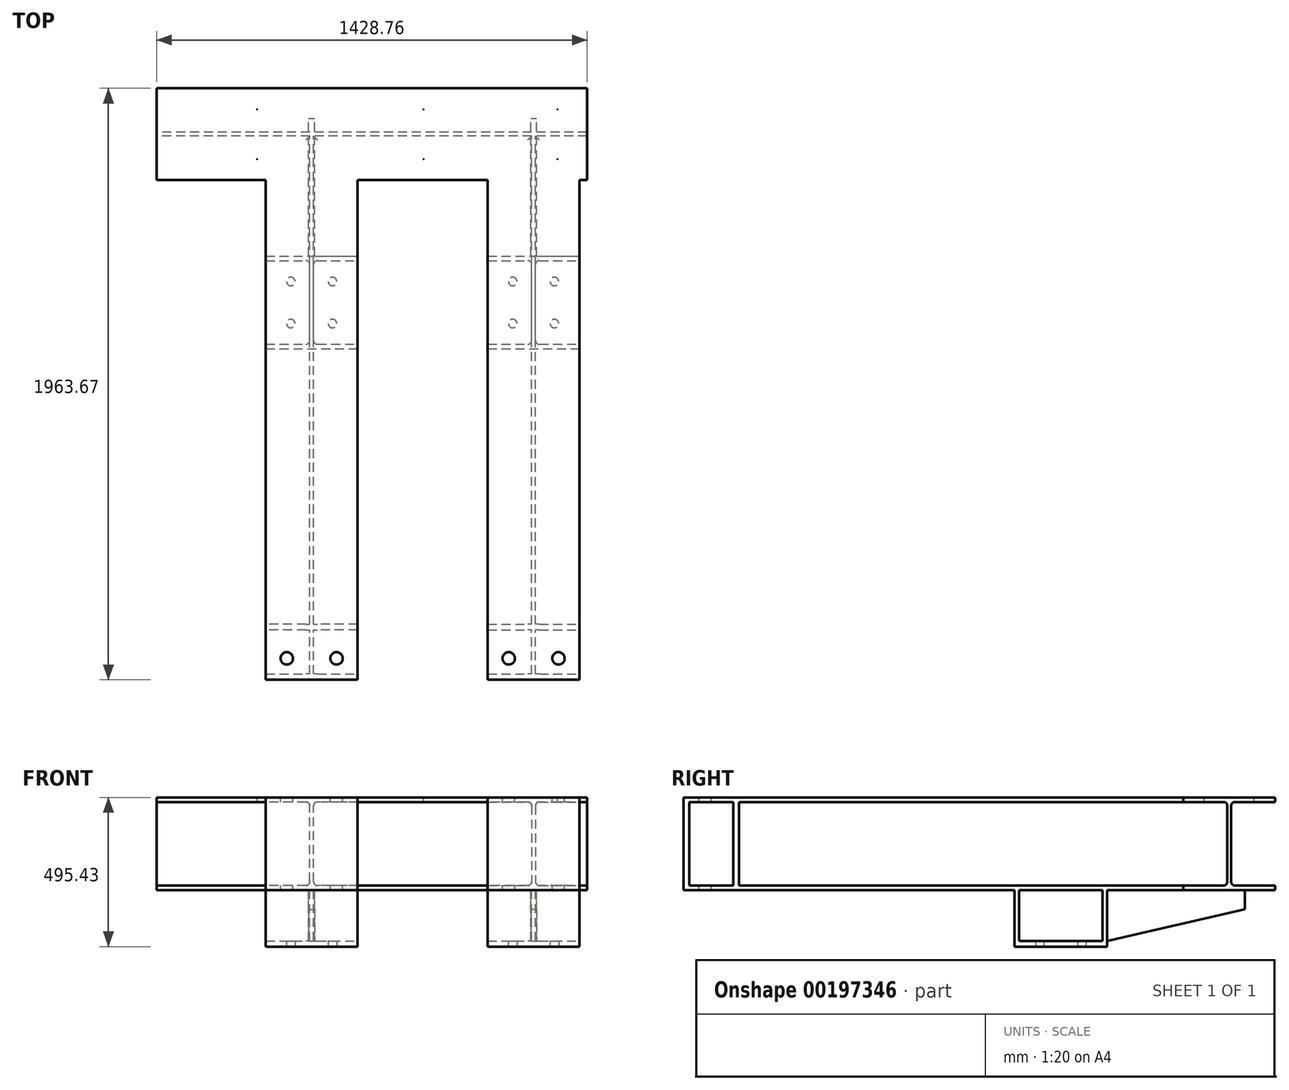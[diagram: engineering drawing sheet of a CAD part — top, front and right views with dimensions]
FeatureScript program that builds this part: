
annotation { "Feature Type Name" : "Feature", "Feature Type Description" : "" }
export const myFeature = defineFeature(function(context is Context, id is Id, definition is map)
    precondition{}
    {
        {
            var Q0;
            Q0=qCreatedBy(makeId("Right.planeOp"),FACE);
            var sketch = newSketch(context, id + "F0", { "sketchPlane" : qUnion([Q0])});
            skLineSegment(sketch, "E0.bottom", {"start": v(-152.4, 153.99) * mm, "end": v(152.4, 153.99) * mm});
            skLineSegment(sketch, "E0.top", {"start": v(-152.4, -153.99) * mm, "end": v(152.4, -153.99) * mm});
            skLineSegment(sketch, "E0.left", {"start": v(-152.4, 153.99) * mm, "end": v(-152.4, 138.75) * mm});
            skLineSegment(sketch, "E0.right", {"start": v(152.4, 153.99) * mm, "end": v(152.4, 138.75) * mm});
            skPoint(sketch, "E0.middle", {"position": v(0, 0) * mm});
            skLineSegment(sketch, "E1.0", {"start": v(-152.4, 138.75) * mm, "end": v(-19.05, 138.75) * mm});
            skLineSegment(sketch, "E2", {"start": v(-217.51, 0) * mm, "end": v(206.8, 0) * mm, "construction": true});
            skPoint(sketch, "E2.startSnap0", {"position": v(-152.4, 0) * mm});
            skLineSegment(sketch, "E3.MirrorCS", {"start": v(-152.4, -138.75) * mm, "end": v(-19.05, -138.75) * mm});
            skLineSegment(sketch, "E4", {"start": v(0, 208.18) * mm, "end": v(0, -222.4) * mm, "construction": true});
            skLineSegment(sketch, "E5.0", {"start": v(-6.35, 126.05) * mm, "end": v(-6.35, -126.05) * mm});
            skLineSegment(sketch, "E6.MirrorCS", {"start": v(6.35, 126.05) * mm, "end": v(6.35, -126.05) * mm});
            skPoint(sketch, "E7.orphan", {"position": v(-6.35, 208.18) * mm});
            skPoint(sketch, "E8.orphan", {"position": v(6.35, 208.18) * mm});
            skLineSegment(sketch, "E9.trimOffspring", {"start": v(19.05, 138.75) * mm, "end": v(152.4, 138.75) * mm});
            skPoint(sketch, "E10.orphan", {"position": v(6.35, -222.4) * mm});
            skLineSegment(sketch, "E11.trimOffspring", {"start": v(19.05, -138.75) * mm, "end": v(152.4, -138.75) * mm});
            skPoint(sketch, "E12.trimOffspring.end.orphan", {"position": v(-6.35, -222.4) * mm});
            skLineSegment(sketch, "E13.trimOffspring", {"start": v(152.4, -138.75) * mm, "end": v(152.4, -153.99) * mm});
            skLineSegment(sketch, "E14.trimOffspring", {"start": v(-152.4, -138.75) * mm, "end": v(-152.4, -153.99) * mm});
            skArc(sketch, "E15.filletArc", {"start": v(-6.35, 126.05) * mm, "mid": v(-10.07, 135.03) * mm, "end": v(-19.05, 138.75) * mm});
            skPoint(sketch, "E16.visualSharp", {"position": v(6.35, 138.75) * mm});
            skArc(sketch, "E16.filletArc", {"start": v(19.05, 138.75) * mm, "mid": v(10.07, 135.03) * mm, "end": v(6.35, 126.05) * mm});
            skPoint(sketch, "E17.visualSharp", {"position": v(6.35, -138.75) * mm});
            skArc(sketch, "E17.filletArc", {"start": v(6.35, -126.05) * mm, "mid": v(10.07, -135.03) * mm, "end": v(19.05, -138.75) * mm});
            skArc(sketch, "E18.filletArc", {"start": v(-19.05, -138.75) * mm, "mid": v(-10.07, -135.03) * mm, "end": v(-6.35, -126.05) * mm});
            skSolve(sketch);
        }
        {
            var Q0;
            Q0 = qSketchRegion(id + "F0", true);
            extrude(context, id + "F1", {"entities" : qUnion([Q0]), "endBound" : BoundingType.SYMMETRIC, "depth" : 1428.75 * mm});
        }
        {
            var Q0;
            Q0=makeQuery(id+"F1.opExtrude","SWEPT_FACE",FACE,{"disambiguationData":[OSD([sQuery(id+"F0.wireOp",EDGE,"E0.bottom")])]});
            var sketch = newSketch(context, id + "F2", { "sketchPlane" : qUnion([Q0])});
            skLineSegment(sketch, "E19.0", {"start": v(-714.38, -152.4) * mm, "end": v(-714.38, 152.4) * mm, "construction": true});
            skLineSegment(sketch, "E20", {"start": v(-714.38, 0) * mm, "end": v(783.99, 0) * mm, "construction": true});
            skLineSegment(sketch, "E21.0", {"start": v(-381, -152.4) * mm, "end": v(-381, 152.4) * mm, "construction": true});
            skLineSegment(sketch, "E22.0", {"start": v(171.45, -152.4) * mm, "end": v(171.45, 152.4) * mm, "construction": true});
            skLineSegment(sketch, "E23.0", {"start": v(615.95, -152.4) * mm, "end": v(615.95, 152.4) * mm, "construction": true});
            skLineSegment(sketch, "E24.0", {"start": v(-714.38, -82.55) * mm, "end": v(783.99, -82.55) * mm, "construction": true});
            skPoint(sketch, "E25", {"position": v(-381, -82.55) * mm});
            skPoint(sketch, "E26", {"position": v(171.45, -82.55) * mm});
            skPoint(sketch, "E27", {"position": v(615.95, -82.55) * mm});
            skPoint(sketch, "E28.MirrorP", {"position": v(615.95, 82.55) * mm});
            skPoint(sketch, "E29.MirrorP", {"position": v(171.45, 82.55) * mm});
            skPoint(sketch, "E30.MirrorP", {"position": v(-381, 82.55) * mm});
            skSolve(sketch);
        }
        {
            var Q0;
            Q0=sQuery(id+"F2.wireOp",VERTEX,"E30.MirrorP");
            var Q1;
            Q1=sQuery(id+"F2.wireOp",VERTEX,"E25");
            var Q2;
            Q2=sQuery(id+"F2.wireOp",VERTEX,"E29.MirrorP");
            var Q3;
            Q3=sQuery(id+"F2.wireOp",VERTEX,"E26");
            var Q4;
            Q4=sQuery(id+"F2.wireOp",VERTEX,"E28.MirrorP");
            var Q5;
            Q5=sQuery(id+"F2.wireOp",VERTEX,"E27");
            var Q6;
            Q6=makeQuery(id+"F1.opExtrude","SWEPT_BODY",BODY,{"disambiguationData":[OSD([sQuery(id+"F0.wireOp",EDGE,"E0.bottom"),sQuery(id+"F0.wireOp",EDGE,"E0.top"),sQuery(id+"F0.wireOp",EDGE,"E0.left"),sQuery(id+"F0.wireOp",EDGE,"E0.right"),sQuery(id+"F0.wireOp",EDGE,"E1.0"),sQuery(id+"F0.wireOp",EDGE,"E3.MirrorCS"),sQuery(id+"F0.wireOp",EDGE,"E5.0"),sQuery(id+"F0.wireOp",EDGE,"E6.MirrorCS"),sQuery(id+"F0.wireOp",EDGE,"E9.trimOffspring"),sQuery(id+"F0.wireOp",EDGE,"E11.trimOffspring"),sQuery(id+"F0.wireOp",EDGE,"E13.trimOffspring"),sQuery(id+"F0.wireOp",EDGE,"E14.trimOffspring"),sQuery(id+"F0.wireOp",EDGE,"E15.filletArc"),sQuery(id+"F0.wireOp",EDGE,"E16.filletArc"),sQuery(id+"F0.wireOp",EDGE,"E17.filletArc"),sQuery(id+"F0.wireOp",EDGE,"E18.filletArc")])]});
            hole(context, id + "F3", {"style" : HoleStyle.SIMPLE, "endStyle" : HoleEndStyle.BLIND, "standardTappedOrClearance" : lookupTablePath({ "standard" : "ANSI", "size" : "7/8", "type" : "Drilled" }), "standardBlindInLast" : lookupTablePath({ "standard" : "ANSI", "size" : "7/8", "type" : "Drilled" }), "holeDiameter" : 7 / 203.2 * mm, "holeDepth" : 76.2 * mm, "locations" : qUnion([Q0, Q1, Q2, Q3, Q4, Q5]), "scope" : qUnion([Q6])});
        }
        {
            var Q0;
            Q0=qCreatedBy(makeId("Front.planeOp"),FACE);
            var sketch = newSketch(context, id + "F4", { "sketchPlane" : qUnion([Q0])});
            skLineSegment(sketch, "E31.0", {"start": v(-714.38, 126.05) * mm, "end": v(-714.38, -126.05) * mm, "construction": true});
            skLineSegment(sketch, "E32.0", {"start": v(714.38, 138.75) * mm, "end": v(-193.68, 138.75) * mm, "construction": true});
            skLineSegment(sketch, "E33.0", {"start": v(714.38, -138.75) * mm, "end": v(-193.68, -138.75) * mm, "construction": true});
            skLineSegment(sketch, "E34.0", {"start": v(714.38, -153.99) * mm, "end": v(-714.38, -153.99) * mm, "construction": true});
            skLineSegment(sketch, "E35.0", {"start": v(714.38, 153.99) * mm, "end": v(-714.38, 153.99) * mm, "construction": true});
            skLineSegment(sketch, "E36", {"start": v(-714.38, 0) * mm, "end": v(832.86, 0) * mm, "construction": true});
            skPoint(sketch, "E36.endSnap0", {"position": v(-714.38, 0) * mm});
            skLineSegment(sketch, "E37.0", {"start": v(-200.03, 126.05) * mm, "end": v(-200.03, -126.05) * mm, "construction": true});
            skLineSegment(sketch, "E38.0", {"start": v(536.58, 126.05) * mm, "end": v(536.58, -126.05) * mm, "construction": true});
            skLineSegment(sketch, "E39.bottom", {"start": v(-352.43, 153.99) * mm, "end": v(-47.62, 153.99) * mm});
            skLineSegment(sketch, "E39.top", {"start": v(-352.43, -153.99) * mm, "end": v(-47.62, -153.99) * mm});
            skLineSegment(sketch, "E39.left", {"start": v(-352.43, 153.99) * mm, "end": v(-352.43, 138.75) * mm});
            skLineSegment(sketch, "E39.right", {"start": v(-47.62, 153.99) * mm, "end": v(-47.62, 138.75) * mm});
            skPoint(sketch, "E39.middle", {"position": v(-200.03, 0) * mm});
            skLineSegment(sketch, "E40", {"start": v(-352.43, 138.75) * mm, "end": v(-219.07, 138.75) * mm});
            skLineSegment(sketch, "E41", {"start": v(-352.43, -138.75) * mm, "end": v(-219.07, -138.75) * mm});
            skLineSegment(sketch, "E42.0", {"start": v(-206.38, 126.05) * mm, "end": v(-206.38, -126.05) * mm});
            skLineSegment(sketch, "E43.MirrorCS", {"start": v(-193.68, 126.05) * mm, "end": v(-193.68, -126.05) * mm});
            skLineSegment(sketch, "E44.trimOffspring", {"start": v(-47.62, -138.75) * mm, "end": v(-180.98, -138.75) * mm, "construction": true});
            skPoint(sketch, "E45.visualSharp", {"position": v(-206.38, 138.75) * mm});
            skArc(sketch, "E45.filletArc", {"start": v(-206.38, 126.05) * mm, "mid": v(-210.1, 135.03) * mm, "end": v(-219.07, 138.75) * mm});
            skPoint(sketch, "E46.orphan", {"position": v(-714.38, 138.75) * mm});
            skPoint(sketch, "E47.orphan", {"position": v(-714.38, -138.75) * mm});
            skLineSegment(sketch, "E48.trimOffspring", {"start": v(-180.98, 138.75) * mm, "end": v(-47.62, 138.75) * mm, "construction": true});
            skLineSegment(sketch, "E49.trimOffspring", {"start": v(-193.68, 138.75) * mm, "end": v(-47.62, 138.75) * mm});
            skLineSegment(sketch, "E50.trimOffspring", {"start": v(-193.68, -138.75) * mm, "end": v(-47.62, -138.75) * mm});
            skPoint(sketch, "E51.visualSharp", {"position": v(-206.38, -138.75) * mm});
            skArc(sketch, "E51.filletArc", {"start": v(-219.07, -138.75) * mm, "mid": v(-210.1, -135.03) * mm, "end": v(-206.38, -126.05) * mm});
            skPoint(sketch, "E52.visualSharp", {"position": v(-193.68, -138.75) * mm});
            skArc(sketch, "E52.filletArc", {"start": v(-193.68, -126.05) * mm, "mid": v(-189.96, -135.03) * mm, "end": v(-180.98, -138.75) * mm});
            skPoint(sketch, "E53.visualSharp", {"position": v(-193.68, 138.75) * mm});
            skArc(sketch, "E53.filletArc", {"start": v(-180.98, 138.75) * mm, "mid": v(-189.96, 135.03) * mm, "end": v(-193.68, 126.05) * mm});
            skLineSegment(sketch, "E54.trimOffspring", {"start": v(-352.43, 0) * mm, "end": v(-352.43, -153.99) * mm});
            skLineSegment(sketch, "E55.trimOffspring", {"start": v(-47.62, 0) * mm, "end": v(-47.62, -153.99) * mm});
            skLineSegment(sketch, "E56.1.0.0", {"start": v(384.17, 153.99) * mm, "end": v(688.97, 153.99) * mm});
            skLineSegment(sketch, "E56.1.0.1", {"start": v(384.17, 0) * mm, "end": v(384.17, -153.99) * mm});
            skLineSegment(sketch, "E56.1.0.2", {"start": v(542.92, 126.05) * mm, "end": v(542.92, -126.05) * mm});
            skLineSegment(sketch, "E56.1.0.3", {"start": v(384.17, -138.75) * mm, "end": v(517.52, -138.75) * mm});
            skLineSegment(sketch, "E56.1.0.4", {"start": v(530.22, 126.05) * mm, "end": v(530.22, -126.05) * mm});
            skLineSegment(sketch, "E56.1.0.5", {"start": v(555.62, 138.75) * mm, "end": v(688.98, 138.75) * mm, "construction": true});
            skPoint(sketch, "E56.1.0.6", {"position": v(542.92, 138.75) * mm});
            skLineSegment(sketch, "E56.1.0.7", {"start": v(536.57, 126.05) * mm, "end": v(536.57, -126.05) * mm, "construction": true});
            skLineSegment(sketch, "E56.1.0.8", {"start": v(384.17, -153.99) * mm, "end": v(688.97, -153.99) * mm});
            skLineSegment(sketch, "E56.1.0.9", {"start": v(384.17, 138.75) * mm, "end": v(517.52, 138.75) * mm});
            skPoint(sketch, "E56.1.0.10", {"position": v(530.22, 138.75) * mm});
            skPoint(sketch, "E56.1.0.11", {"position": v(536.57, 0) * mm});
            skPoint(sketch, "E56.1.0.12", {"position": v(530.22, -138.75) * mm});
            skPoint(sketch, "E56.1.0.13", {"position": v(542.92, -138.75) * mm});
            skLineSegment(sketch, "E56.1.0.14", {"start": v(688.98, -138.75) * mm, "end": v(555.62, -138.75) * mm, "construction": true});
            skLineSegment(sketch, "E56.1.0.15", {"start": v(688.97, 0) * mm, "end": v(688.97, -153.99) * mm});
            skLineSegment(sketch, "E56.1.0.16", {"start": v(542.92, 138.75) * mm, "end": v(688.97, 138.75) * mm});
            skLineSegment(sketch, "E56.1.0.17", {"start": v(542.92, -138.75) * mm, "end": v(688.97, -138.75) * mm});
            skLineSegment(sketch, "E56.1.0.18", {"start": v(384.17, 153.99) * mm, "end": v(384.17, 138.75) * mm});
            skArc(sketch, "E56.1.0.19", {"start": v(530.22, 126.05) * mm, "mid": v(526.5, 135.03) * mm, "end": v(517.52, 138.75) * mm});
            skLineSegment(sketch, "E56.1.0.20", {"start": v(688.97, 153.99) * mm, "end": v(688.97, 138.75) * mm});
            skArc(sketch, "E56.1.0.21", {"start": v(542.92, -126.05) * mm, "mid": v(546.64, -135.03) * mm, "end": v(555.62, -138.75) * mm});
            skArc(sketch, "E56.1.0.22", {"start": v(517.52, -138.75) * mm, "mid": v(526.5, -135.03) * mm, "end": v(530.22, -126.05) * mm});
            skArc(sketch, "E56.1.0.23", {"start": v(555.62, 138.75) * mm, "mid": v(546.64, 135.03) * mm, "end": v(542.92, 126.05) * mm});
            skLineSegment(sketch, "E56.direction1", {"start": v(-352.43, -153.99) * mm, "end": v(384.17, -153.99) * mm, "construction": true});
            skSolve(sketch);
        }
        {
            var Q0;
            Q0 = qSketchRegion(id + "F4", true);
            extrude(context, id + "F5", {"entities" : qUnion([Q0]), "depth" : 1792.22 * mm});
        }
        {
            var Q0;
            Q0=makeQuery(id+"F5.opExtrude","CAP_FACE",FACE,{"disambiguationData":[OSD([sQuery(id+"F4.wireOp",EDGE,"E39.bottom"),sQuery(id+"F4.wireOp",EDGE,"E39.top"),sQuery(id+"F4.wireOp",EDGE,"E39.left"),sQuery(id+"F4.wireOp",EDGE,"E39.right"),sQuery(id+"F4.wireOp",EDGE,"E40"),sQuery(id+"F4.wireOp",EDGE,"E41"),sQuery(id+"F4.wireOp",EDGE,"E42.0"),sQuery(id+"F4.wireOp",EDGE,"E43.MirrorCS"),sQuery(id+"F4.wireOp",EDGE,"E45.filletArc"),sQuery(id+"F4.wireOp",EDGE,"E49.trimOffspring"),sQuery(id+"F4.wireOp",EDGE,"E50.trimOffspring"),sQuery(id+"F4.wireOp",EDGE,"E51.filletArc"),sQuery(id+"F4.wireOp",EDGE,"E52.filletArc"),sQuery(id+"F4.wireOp",EDGE,"E53.filletArc"),sQuery(id+"F4.wireOp",EDGE,"E54.trimOffspring"),sQuery(id+"F4.wireOp",EDGE,"E55.trimOffspring")])],"isStart":false});
            var sketch = newSketch(context, id + "F6", { "sketchPlane" : qUnion([Q0])});
            skLineSegment(sketch, "E57.bottom", {"start": v(-352.43, 153.99) * mm, "end": v(-47.62, 153.99) * mm});
            skLineSegment(sketch, "E57.top", {"start": v(-352.43, -153.99) * mm, "end": v(-47.62, -153.99) * mm});
            skLineSegment(sketch, "E57.left", {"start": v(-352.43, 153.99) * mm, "end": v(-352.43, -153.99) * mm});
            skLineSegment(sketch, "E57.right", {"start": v(-47.62, 153.99) * mm, "end": v(-47.62, -153.99) * mm});
            skLineSegment(sketch, "E58.1.0.0", {"start": v(384.18, 153.99) * mm, "end": v(688.98, 153.99) * mm});
            skLineSegment(sketch, "E58.1.0.1", {"start": v(384.18, -153.99) * mm, "end": v(688.98, -153.99) * mm});
            skLineSegment(sketch, "E58.1.0.2", {"start": v(384.18, 153.99) * mm, "end": v(384.18, -153.99) * mm});
            skLineSegment(sketch, "E58.1.0.3", {"start": v(688.98, 153.99) * mm, "end": v(688.98, -153.99) * mm});
            skLineSegment(sketch, "E58.direction1", {"start": v(-352.43, -153.99) * mm, "end": v(384.18, -153.99) * mm, "construction": true});
            skSolve(sketch);
        }
        {
            var Q0;
            Q0 = qSketchRegion(id + "F6", true);
            extrude(context, id + "F7", {"entities" : qUnion([Q0]), "depth" : 19.05 * mm});
        }
        {
            var Q0;
            Q0=makeQuery(id+"F1.opExtrude","SWEPT_BODY",BODY,{"disambiguationData":[OSD([sQuery(id+"F0.wireOp",EDGE,"E0.bottom"),sQuery(id+"F0.wireOp",EDGE,"E0.top"),sQuery(id+"F0.wireOp",EDGE,"E0.left"),sQuery(id+"F0.wireOp",EDGE,"E0.right"),sQuery(id+"F0.wireOp",EDGE,"E1.0"),sQuery(id+"F0.wireOp",EDGE,"E3.MirrorCS"),sQuery(id+"F0.wireOp",EDGE,"E5.0"),sQuery(id+"F0.wireOp",EDGE,"E6.MirrorCS"),sQuery(id+"F0.wireOp",EDGE,"E9.trimOffspring"),sQuery(id+"F0.wireOp",EDGE,"E11.trimOffspring"),sQuery(id+"F0.wireOp",EDGE,"E13.trimOffspring"),sQuery(id+"F0.wireOp",EDGE,"E14.trimOffspring"),sQuery(id+"F0.wireOp",EDGE,"E15.filletArc"),sQuery(id+"F0.wireOp",EDGE,"E16.filletArc"),sQuery(id+"F0.wireOp",EDGE,"E17.filletArc"),sQuery(id+"F0.wireOp",EDGE,"E18.filletArc")])]});
            var Q1;
            Q1=makeQuery(id+"F5.opExtrude","SWEPT_BODY",BODY,{"disambiguationData":[OSD([sQuery(id+"F4.wireOp",EDGE,"E39.bottom"),sQuery(id+"F4.wireOp",EDGE,"E39.top"),sQuery(id+"F4.wireOp",EDGE,"E39.left"),sQuery(id+"F4.wireOp",EDGE,"E39.right"),sQuery(id+"F4.wireOp",EDGE,"E40"),sQuery(id+"F4.wireOp",EDGE,"E41"),sQuery(id+"F4.wireOp",EDGE,"E42.0"),sQuery(id+"F4.wireOp",EDGE,"E43.MirrorCS"),sQuery(id+"F4.wireOp",EDGE,"E45.filletArc"),sQuery(id+"F4.wireOp",EDGE,"E49.trimOffspring"),sQuery(id+"F4.wireOp",EDGE,"E50.trimOffspring"),sQuery(id+"F4.wireOp",EDGE,"E51.filletArc"),sQuery(id+"F4.wireOp",EDGE,"E52.filletArc"),sQuery(id+"F4.wireOp",EDGE,"E53.filletArc"),sQuery(id+"F4.wireOp",EDGE,"E54.trimOffspring"),sQuery(id+"F4.wireOp",EDGE,"E55.trimOffspring")])]});
            var Q2;
            Q2=makeQuery(id+"F5.opExtrude","SWEPT_BODY",BODY,{"disambiguationData":[OSD([sQuery(id+"F4.wireOp",EDGE,"E56.1.0.0"),sQuery(id+"F4.wireOp",EDGE,"E56.1.0.1"),sQuery(id+"F4.wireOp",EDGE,"E56.1.0.2"),sQuery(id+"F4.wireOp",EDGE,"E56.1.0.3"),sQuery(id+"F4.wireOp",EDGE,"E56.1.0.4"),sQuery(id+"F4.wireOp",EDGE,"E56.1.0.8"),sQuery(id+"F4.wireOp",EDGE,"E56.1.0.9"),sQuery(id+"F4.wireOp",EDGE,"E56.1.0.15"),sQuery(id+"F4.wireOp",EDGE,"E56.1.0.16"),sQuery(id+"F4.wireOp",EDGE,"E56.1.0.17"),sQuery(id+"F4.wireOp",EDGE,"E56.1.0.18"),sQuery(id+"F4.wireOp",EDGE,"E56.1.0.19"),sQuery(id+"F4.wireOp",EDGE,"E56.1.0.20"),sQuery(id+"F4.wireOp",EDGE,"E56.1.0.21"),sQuery(id+"F4.wireOp",EDGE,"E56.1.0.22"),sQuery(id+"F4.wireOp",EDGE,"E56.1.0.23")])]});
            var Q3;
            Q3=makeQuery(id+"F7.opExtrude","SWEPT_BODY",BODY,{"disambiguationData":[OSD([sQuery(id+"F6.wireOp",EDGE,"E58.1.0.0"),sQuery(id+"F6.wireOp",EDGE,"E58.1.0.1"),sQuery(id+"F6.wireOp",EDGE,"E58.1.0.2"),sQuery(id+"F6.wireOp",EDGE,"E58.1.0.3")])]});
            var Q4;
            Q4=makeQuery(id+"F7.opExtrude","SWEPT_BODY",BODY,{"disambiguationData":[OSD([sQuery(id+"F6.wireOp",EDGE,"E57.bottom"),sQuery(id+"F6.wireOp",EDGE,"E57.top"),sQuery(id+"F6.wireOp",EDGE,"E57.left"),sQuery(id+"F6.wireOp",EDGE,"E57.right")])]});
            booleanBodies(context, id + "F8", {"operationType" : BooleanOperationType.UNION, "tools" : qUnion([Q0, Q1, Q2, Q3, Q4])});
        }
        {
            var Q0;
            Q0=makeQuery(id+"F8.opBoolean","MERGE",FACE,{"derivedFrom":[makeQuery(id+"F1.opExtrude","SWEPT_FACE",FACE,{"disambiguationData":[OSD([sQuery(id+"F0.wireOp",EDGE,"E0.bottom")])]}),makeQuery(id+"F5.opExtrude","SWEPT_FACE",FACE,{"disambiguationData":[OSD([sQuery(id+"F4.wireOp",EDGE,"E39.bottom")])]}),makeQuery(id+"F5.opExtrude","SWEPT_FACE",FACE,{"disambiguationData":[OSD([sQuery(id+"F4.wireOp",EDGE,"E56.1.0.0")])]}),makeQuery(id+"F7.opExtrude","SWEPT_FACE",FACE,{"disambiguationData":[OSD([sQuery(id+"F6.wireOp",EDGE,"E57.bottom")])]}),makeQuery(id+"F7.opExtrude","SWEPT_FACE",FACE,{"disambiguationData":[OSD([sQuery(id+"F6.wireOp",EDGE,"E58.1.0.0")])]})]});
            var sketch = newSketch(context, id + "F9", { "sketchPlane" : qUnion([Q0])});
            skLineSegment(sketch, "E59", {"start": v(-857.12, 0) * mm, "end": v(851.08, 0) * mm, "construction": true});
            skCircle(sketch, "E60.0", {"center": v(615.95, 82.55) * mm, "radius": 11.11 * mm});
            skCircle(sketch, "E61.MirrorC", {"center": v(615.95, -82.55) * mm, "radius": 11.11 * mm});
            skSolve(sketch);
        }
        {
            var Q0;
            Q0=sQuery(id+"F9.wireOp",VERTEX,"E61.MirrorC.center");
            var Q1;
            Q1=makeQuery(id+"F1.opExtrude","SWEPT_BODY",BODY,{"disambiguationData":[OSD([sQuery(id+"F0.wireOp",EDGE,"E0.bottom"),sQuery(id+"F0.wireOp",EDGE,"E0.top"),sQuery(id+"F0.wireOp",EDGE,"E0.left"),sQuery(id+"F0.wireOp",EDGE,"E0.right"),sQuery(id+"F0.wireOp",EDGE,"E1.0"),sQuery(id+"F0.wireOp",EDGE,"E3.MirrorCS"),sQuery(id+"F0.wireOp",EDGE,"E5.0"),sQuery(id+"F0.wireOp",EDGE,"E6.MirrorCS"),sQuery(id+"F0.wireOp",EDGE,"E9.trimOffspring"),sQuery(id+"F0.wireOp",EDGE,"E11.trimOffspring"),sQuery(id+"F0.wireOp",EDGE,"E13.trimOffspring"),sQuery(id+"F0.wireOp",EDGE,"E14.trimOffspring"),sQuery(id+"F0.wireOp",EDGE,"E15.filletArc"),sQuery(id+"F0.wireOp",EDGE,"E16.filletArc"),sQuery(id+"F0.wireOp",EDGE,"E17.filletArc"),sQuery(id+"F0.wireOp",EDGE,"E18.filletArc")])]});
            hole(context, id + "F10", {"style" : HoleStyle.SIMPLE, "endStyle" : HoleEndStyle.BLIND, "standardTappedOrClearance" : lookupTablePath({ "standard" : "ANSI", "size" : "7/8", "type" : "Drilled" }), "standardBlindInLast" : lookupTablePath({ "standard" : "ANSI", "size" : "7/8", "type" : "Drilled" }), "holeDiameter" : 7 / 203.2 * mm, "holeDepth" : 76.2 * mm, "locations" : qUnion([Q0]), "scope" : qUnion([Q1])});
        }
        {
            var Q0;
            Q0=makeQuery(id+"F8.opBoolean","MERGE",FACE,{"derivedFrom":[makeQuery(id+"F5.opExtrude","SWEPT_FACE",FACE,{"disambiguationData":[OSD([sQuery(id+"F4.wireOp",EDGE,"E56.1.0.15")])]}),makeQuery(id+"F5.opExtrude","SWEPT_FACE",FACE,{"disambiguationData":[OSD([sQuery(id+"F4.wireOp",EDGE,"E56.1.0.20")])]}),makeQuery(id+"F7.opExtrude","SWEPT_FACE",FACE,{"disambiguationData":[OSD([sQuery(id+"F6.wireOp",EDGE,"E58.1.0.3")])]})]});
            var sketch = newSketch(context, id + "F11", { "sketchPlane" : qUnion([Q0])});
            skLineSegment(sketch, "E62.0.0", {"start": v(-6.35, -126.05) * mm, "end": v(-6.35, 126.05) * mm, "construction": true});
            skLineSegment(sketch, "E62.0.1", {"start": v(-6.35, 126.05) * mm, "end": v(-19.05, 126.05) * mm, "construction": true});
            skLineSegment(sketch, "E62.0.2", {"start": v(-1792.22, 126.05) * mm, "end": v(-1792.22, -126.05) * mm, "construction": true});
            skLineSegment(sketch, "E63.0", {"start": v(-1646.17, 138.75) * mm, "end": v(-1646.17, -138.75) * mm});
            skLineSegment(sketch, "E64.0.0", {"start": v(-19.05, 126.05) * mm, "end": v(-6.35, 126.05) * mm});
            skArc(sketch, "E64.0.1", {"start": v(-6.35, 126.05) * mm, "mid": v(-10.07, 135.03) * mm, "end": v(-19.05, 138.75) * mm});
            skLineSegment(sketch, "E64.0.2", {"start": v(-19.05, 138.75) * mm, "end": v(-1792.22, 138.75) * mm});
            skLineSegment(sketch, "E64.0.3", {"start": v(-1792.22, 138.75) * mm, "end": v(-1792.22, 126.05) * mm});
            skLineSegment(sketch, "E65.0.0", {"start": v(-1792.22, -138.75) * mm, "end": v(-19.05, -138.75) * mm});
            skArc(sketch, "E65.0.1", {"start": v(-19.05, -138.75) * mm, "mid": v(-10.07, -135.03) * mm, "end": v(-6.35, -126.05) * mm});
            skLineSegment(sketch, "E65.0.2", {"start": v(-6.35, -126.05) * mm, "end": v(-19.05, -126.05) * mm});
            skLineSegment(sketch, "E65.0.3", {"start": v(-1792.22, -126.05) * mm, "end": v(-1792.22, -138.75) * mm});
            skLineSegment(sketch, "E66.trimOffspring", {"start": v(-19.05, -126.05) * mm, "end": v(-6.35, -126.05) * mm, "construction": true});
            skLineSegment(sketch, "E67.0", {"start": v(-1627.12, 138.75) * mm, "end": v(-1627.12, -138.75) * mm});
            skSolve(sketch);
        }
        {
            var Q0;
            Q0 = qSketchRegion(id + "F11", true);
            extrude(context, id + "F12", {"entities" : qUnion([Q0]), "operationType" : NewBodyOperationType.ADD, "oppositeDirection" : true, "depth" : 304.8 * mm});
        }
        {
            var Q0;
            Q0=makeQuery(id+"F8.opBoolean","MERGE",FACE,{"derivedFrom":[makeQuery(id+"F5.opExtrude","SWEPT_FACE",FACE,{"disambiguationData":[OSD([sQuery(id+"F4.wireOp",EDGE,"E39.left")])]}),makeQuery(id+"F5.opExtrude","SWEPT_FACE",FACE,{"disambiguationData":[OSD([sQuery(id+"F4.wireOp",EDGE,"E54.trimOffspring")])]}),makeQuery(id+"F7.opExtrude","SWEPT_FACE",FACE,{"disambiguationData":[OSD([sQuery(id+"F6.wireOp",EDGE,"E57.left")])]})]});
            var sketch = newSketch(context, id + "F13", { "sketchPlane" : qUnion([Q0])});
            skLineSegment(sketch, "E68.0", {"start": v(1646.17, 138.75) * mm, "end": v(1646.17, -138.75) * mm});
            skLineSegment(sketch, "E69.0", {"start": v(1627.12, 138.75) * mm, "end": v(1627.12, -138.75) * mm});
            skLineSegment(sketch, "E70.bottom", {"start": v(1627.12, 138.75) * mm, "end": v(1646.17, 138.75) * mm});
            skLineSegment(sketch, "E70.top", {"start": v(1627.12, -138.75) * mm, "end": v(1646.17, -138.75) * mm});
            skSolve(sketch);
        }
        {
            var Q0;
            Q0 = qSketchRegion(id + "F13", true);
            extrude(context, id + "F14", {"entities" : qUnion([Q0]), "operationType" : NewBodyOperationType.ADD, "oppositeDirection" : true, "depth" : 304.8 * mm});
        }
        {
            var Q0;
            Q0=makeQuery(id+"F8.opBoolean","MERGE",FACE,{"derivedFrom":[makeQuery(id+"F1.opExtrude","SWEPT_FACE",FACE,{"disambiguationData":[OSD([sQuery(id+"F0.wireOp",EDGE,"E0.bottom")])]}),makeQuery(id+"F5.opExtrude","SWEPT_FACE",FACE,{"disambiguationData":[OSD([sQuery(id+"F4.wireOp",EDGE,"E39.bottom")])]}),makeQuery(id+"F5.opExtrude","SWEPT_FACE",FACE,{"disambiguationData":[OSD([sQuery(id+"F4.wireOp",EDGE,"E56.1.0.0")])]}),makeQuery(id+"F7.opExtrude","SWEPT_FACE",FACE,{"disambiguationData":[OSD([sQuery(id+"F6.wireOp",EDGE,"E57.bottom")])]}),makeQuery(id+"F7.opExtrude","SWEPT_FACE",FACE,{"disambiguationData":[OSD([sQuery(id+"F6.wireOp",EDGE,"E58.1.0.0")])]})]});
            var sketch = newSketch(context, id + "F15", { "sketchPlane" : qUnion([Q0])});
            skLineSegment(sketch, "E71.0", {"start": v(714.38, 152.4) * mm, "end": v(-714.38, 152.4) * mm, "construction": true});
            skLineSegment(sketch, "E72.0", {"start": v(714.38, -1739.9) * mm, "end": v(-714.38, -1739.9) * mm, "construction": true});
            skLineSegment(sketch, "E73.0", {"start": v(384.18, -1811.27) * mm, "end": v(688.98, -1811.27) * mm, "construction": true});
            skLineSegment(sketch, "E74.0", {"start": v(-352.43, -1811.27) * mm, "end": v(-47.62, -1811.27) * mm, "construction": true});
            skLineSegment(sketch, "E75", {"start": v(536.58, -1811.27) * mm, "end": v(536.58, 289.08) * mm, "construction": true});
            skLineSegment(sketch, "E76", {"start": v(-200.02, -1811.27) * mm, "end": v(-200.02, 297.75) * mm, "construction": true});
            skLineSegment(sketch, "E77.0", {"start": v(619.12, -1811.27) * mm, "end": v(619.12, 289.08) * mm, "construction": true});
            skLineSegment(sketch, "E78.0", {"start": v(-117.47, -1811.27) * mm, "end": v(-117.47, 297.75) * mm, "construction": true});
            skPoint(sketch, "E79", {"position": v(619.12, -1739.9) * mm});
            skPoint(sketch, "E80", {"position": v(-117.47, -1739.9) * mm});
            skPoint(sketch, "E81.MirrorP", {"position": v(454.03, -1739.9) * mm});
            skPoint(sketch, "E82.MirrorP", {"position": v(-282.57, -1739.9) * mm});
            skSolve(sketch);
        }
        {
            var Q0;
            Q0=sQuery(id+"F15.wireOp",VERTEX,"E79");
            var Q1;
            Q1=sQuery(id+"F15.wireOp",VERTEX,"E81.MirrorP");
            var Q2;
            Q2=sQuery(id+"F15.wireOp",VERTEX,"E80");
            var Q3;
            Q3=sQuery(id+"F15.wireOp",VERTEX,"E82.MirrorP");
            var Q4;
            Q4=makeQuery(id+"F1.opExtrude","SWEPT_BODY",BODY,{"disambiguationData":[OSD([sQuery(id+"F0.wireOp",EDGE,"E0.bottom"),sQuery(id+"F0.wireOp",EDGE,"E0.top"),sQuery(id+"F0.wireOp",EDGE,"E0.left"),sQuery(id+"F0.wireOp",EDGE,"E0.right"),sQuery(id+"F0.wireOp",EDGE,"E1.0"),sQuery(id+"F0.wireOp",EDGE,"E3.MirrorCS"),sQuery(id+"F0.wireOp",EDGE,"E5.0"),sQuery(id+"F0.wireOp",EDGE,"E6.MirrorCS"),sQuery(id+"F0.wireOp",EDGE,"E9.trimOffspring"),sQuery(id+"F0.wireOp",EDGE,"E11.trimOffspring"),sQuery(id+"F0.wireOp",EDGE,"E13.trimOffspring"),sQuery(id+"F0.wireOp",EDGE,"E14.trimOffspring"),sQuery(id+"F0.wireOp",EDGE,"E15.filletArc"),sQuery(id+"F0.wireOp",EDGE,"E16.filletArc"),sQuery(id+"F0.wireOp",EDGE,"E17.filletArc"),sQuery(id+"F0.wireOp",EDGE,"E18.filletArc")])]});
            hole(context, id + "F16", {"style" : HoleStyle.SIMPLE, "endStyle" : HoleEndStyle.THROUGH, "holeDiameter" : 41.4 * mm, "locations" : qUnion([Q0, Q1, Q2, Q3]), "scope" : qUnion([Q4]), "isTappedThrough" : true});
        }
        {
            var Q0;
            Q0=makeQuery(id+"F8.opBoolean","MERGE",FACE,{"derivedFrom":[makeQuery(id+"F1.opExtrude","SWEPT_FACE",FACE,{"disambiguationData":[OSD([sQuery(id+"F0.wireOp",EDGE,"E0.top")])]}),makeQuery(id+"F5.opExtrude","SWEPT_FACE",FACE,{"disambiguationData":[OSD([sQuery(id+"F4.wireOp",EDGE,"E39.top")])]}),makeQuery(id+"F5.opExtrude","SWEPT_FACE",FACE,{"disambiguationData":[OSD([sQuery(id+"F4.wireOp",EDGE,"E56.1.0.8")])]}),makeQuery(id+"F7.opExtrude","SWEPT_FACE",FACE,{"disambiguationData":[OSD([sQuery(id+"F6.wireOp",EDGE,"E57.top")])]}),makeQuery(id+"F7.opExtrude","SWEPT_FACE",FACE,{"disambiguationData":[OSD([sQuery(id+"F6.wireOp",EDGE,"E58.1.0.1")])]})]});
            var sketch = newSketch(context, id + "F17", { "sketchPlane" : qUnion([Q0])});
            skLineSegment(sketch, "E83.0", {"start": v(714.38, -152.4) * mm, "end": v(-714.38, -152.4) * mm, "construction": true});
            skLineSegment(sketch, "E84.0", {"start": v(714.38, 558.8) * mm, "end": v(-714.38, 558.8) * mm, "construction": true});
            skLineSegment(sketch, "E85.0", {"start": v(-352.43, 1811.27) * mm, "end": v(-47.62, 1811.27) * mm, "construction": true});
            skLineSegment(sketch, "E86.0", {"start": v(384.18, 1811.27) * mm, "end": v(688.98, 1811.27) * mm, "construction": true});
            skLineSegment(sketch, "E87", {"start": v(-200.02, 1811.27) * mm, "end": v(-200.02, -241.76) * mm, "construction": true});
            skLineSegment(sketch, "E88", {"start": v(536.58, 1811.27) * mm, "end": v(536.58, -262.08) * mm, "construction": true});
            skLineSegment(sketch, "E89.bottom", {"start": v(-352.43, 404.88) * mm, "end": v(-47.62, 404.88) * mm});
            skLineSegment(sketch, "E89.top", {"start": v(-352.43, 712.72) * mm, "end": v(-47.62, 712.72) * mm});
            skLineSegment(sketch, "E89.left", {"start": v(-352.43, 404.88) * mm, "end": v(-352.43, 420.12) * mm});
            skLineSegment(sketch, "E89.right", {"start": v(-47.63, 404.88) * mm, "end": v(-47.63, 420.12) * mm});
            skPoint(sketch, "E89.middle", {"position": v(-200.03, 558.8) * mm});
            skLineSegment(sketch, "E90.0", {"start": v(-352.43, 697.48) * mm, "end": v(-219.07, 697.48) * mm});
            skLineSegment(sketch, "E91.0", {"start": v(-352.43, 420.12) * mm, "end": v(-219.07, 420.12) * mm});
            skLineSegment(sketch, "E92.0", {"start": v(-206.37, 684.78) * mm, "end": v(-206.37, 432.82) * mm});
            skLineSegment(sketch, "E93.trimOffspring", {"start": v(-206.37, -152.4) * mm, "end": v(-206.37, -241.76) * mm});
            skLineSegment(sketch, "E94.MirrorCS", {"start": v(-193.67, 684.78) * mm, "end": v(-193.67, 432.82) * mm});
            skLineSegment(sketch, "E95.trimOffspring", {"start": v(-180.97, 420.12) * mm, "end": v(-47.62, 420.12) * mm});
            skLineSegment(sketch, "E96.trimOffspring", {"start": v(-352.43, 558.8) * mm, "end": v(-352.43, 712.72) * mm});
            skLineSegment(sketch, "E97.trimOffspring", {"start": v(-47.63, 558.8) * mm, "end": v(-47.63, 712.72) * mm});
            skLineSegment(sketch, "E98.trimOffspring", {"start": v(-180.97, 697.48) * mm, "end": v(-47.62, 697.48) * mm});
            skPoint(sketch, "E99.newPointA", {"position": v(-206.37, 697.48) * mm});
            skArc(sketch, "E99.filletArc", {"start": v(-206.37, 684.78) * mm, "mid": v(-210.1, 693.76) * mm, "end": v(-219.07, 697.48) * mm});
            skPoint(sketch, "E100.visualSharp", {"position": v(-193.67, 697.48) * mm});
            skArc(sketch, "E100.filletArc", {"start": v(-180.97, 697.48) * mm, "mid": v(-189.96, 693.76) * mm, "end": v(-193.67, 684.78) * mm});
            skPoint(sketch, "E101.newPointA", {"position": v(-206.37, 420.12) * mm});
            skArc(sketch, "E101.filletArc", {"start": v(-219.07, 420.12) * mm, "mid": v(-210.1, 423.84) * mm, "end": v(-206.38, 432.82) * mm});
            skPoint(sketch, "E102.visualSharp", {"position": v(-193.67, 420.12) * mm});
            skArc(sketch, "E102.filletArc", {"start": v(-193.67, 432.82) * mm, "mid": v(-189.96, 423.84) * mm, "end": v(-180.97, 420.12) * mm});
            skLineSegment(sketch, "E103.1.0.0", {"start": v(555.62, 420.12) * mm, "end": v(688.98, 420.12) * mm});
            skLineSegment(sketch, "E103.1.0.1", {"start": v(384.18, 712.72) * mm, "end": v(688.98, 712.72) * mm});
            skLineSegment(sketch, "E103.1.0.2", {"start": v(542.93, 684.78) * mm, "end": v(542.93, 432.82) * mm});
            skLineSegment(sketch, "E103.1.0.3", {"start": v(384.18, 420.12) * mm, "end": v(517.52, 420.12) * mm});
            skLineSegment(sketch, "E103.1.0.4", {"start": v(384.18, 697.48) * mm, "end": v(517.52, 697.48) * mm});
            skLineSegment(sketch, "E103.1.0.5", {"start": v(384.18, 558.8) * mm, "end": v(384.18, 712.72) * mm});
            skLineSegment(sketch, "E103.1.0.6", {"start": v(530.23, 684.78) * mm, "end": v(530.23, 432.82) * mm});
            skLineSegment(sketch, "E103.1.0.7", {"start": v(555.62, 697.48) * mm, "end": v(688.98, 697.48) * mm});
            skLineSegment(sketch, "E103.1.0.8", {"start": v(688.98, 558.8) * mm, "end": v(688.98, 712.72) * mm});
            skPoint(sketch, "E103.1.0.9", {"position": v(536.58, 558.8) * mm});
            skLineSegment(sketch, "E103.1.0.10", {"start": v(384.18, 404.88) * mm, "end": v(688.98, 404.88) * mm});
            skPoint(sketch, "E103.1.0.11", {"position": v(530.23, 697.48) * mm});
            skPoint(sketch, "E103.1.0.12", {"position": v(542.93, 420.12) * mm});
            skPoint(sketch, "E103.1.0.13", {"position": v(530.23, 420.12) * mm});
            skPoint(sketch, "E103.1.0.14", {"position": v(542.93, 697.48) * mm});
            skLineSegment(sketch, "E103.1.0.15", {"start": v(688.98, 404.88) * mm, "end": v(688.98, 420.12) * mm});
            skLineSegment(sketch, "E103.1.0.16", {"start": v(384.18, 404.88) * mm, "end": v(384.18, 420.12) * mm});
            skArc(sketch, "E103.1.0.17", {"start": v(517.53, 420.12) * mm, "mid": v(526.5, 423.84) * mm, "end": v(530.23, 432.82) * mm});
            skArc(sketch, "E103.1.0.18", {"start": v(555.63, 697.48) * mm, "mid": v(546.64, 693.76) * mm, "end": v(542.93, 684.78) * mm});
            skArc(sketch, "E103.1.0.19", {"start": v(530.23, 684.78) * mm, "mid": v(526.5, 693.76) * mm, "end": v(517.53, 697.48) * mm});
            skArc(sketch, "E103.1.0.20", {"start": v(542.93, 432.82) * mm, "mid": v(546.64, 423.84) * mm, "end": v(555.62, 420.12) * mm});
            skLineSegment(sketch, "E103.direction1", {"start": v(-352.43, 404.88) * mm, "end": v(384.18, 404.88) * mm, "construction": true});
            skSolve(sketch);
        }
        {
            var Q0;
            Q0 = qSketchRegion(id + "F17", true);
            extrude(context, id + "F18", {"entities" : qUnion([Q0]), "depth" : 168.4 * mm});
        }
        {
            var Q0;
            Q0=makeQuery(id+"F18.opExtrude","CAP_FACE",FACE,{"disambiguationData":[OSD([sQuery(id+"F17.wireOp",EDGE,"E89.bottom"),sQuery(id+"F17.wireOp",EDGE,"E89.top"),sQuery(id+"F17.wireOp",EDGE,"E89.left"),sQuery(id+"F17.wireOp",EDGE,"E89.right"),sQuery(id+"F17.wireOp",EDGE,"E90.0"),sQuery(id+"F17.wireOp",EDGE,"E91.0"),sQuery(id+"F17.wireOp",EDGE,"E92.0"),sQuery(id+"F17.wireOp",EDGE,"E94.MirrorCS"),sQuery(id+"F17.wireOp",EDGE,"E95.trimOffspring"),sQuery(id+"F17.wireOp",EDGE,"E96.trimOffspring"),sQuery(id+"F17.wireOp",EDGE,"E97.trimOffspring"),sQuery(id+"F17.wireOp",EDGE,"E98.trimOffspring"),sQuery(id+"F17.wireOp",EDGE,"E99.filletArc"),sQuery(id+"F17.wireOp",EDGE,"E100.filletArc"),sQuery(id+"F17.wireOp",EDGE,"E101.filletArc"),sQuery(id+"F17.wireOp",EDGE,"E102.filletArc")])],"isStart":false});
            var sketch = newSketch(context, id + "F19", { "sketchPlane" : qUnion([Q0])});
            skLineSegment(sketch, "E104.bottom", {"start": v(-352.43, 712.72) * mm, "end": v(-47.62, 712.72) * mm});
            skLineSegment(sketch, "E104.top", {"start": v(-352.43, 404.88) * mm, "end": v(-47.62, 404.88) * mm});
            skLineSegment(sketch, "E104.left", {"start": v(-352.43, 712.72) * mm, "end": v(-352.43, 404.88) * mm});
            skLineSegment(sketch, "E104.right", {"start": v(-47.62, 712.72) * mm, "end": v(-47.62, 404.88) * mm});
            skLineSegment(sketch, "E105.1.0.0", {"start": v(384.18, 712.72) * mm, "end": v(688.98, 712.72) * mm});
            skLineSegment(sketch, "E105.1.0.1", {"start": v(384.18, 712.72) * mm, "end": v(384.18, 404.88) * mm});
            skLineSegment(sketch, "E105.1.0.2", {"start": v(384.18, 404.88) * mm, "end": v(688.98, 404.88) * mm});
            skLineSegment(sketch, "E105.1.0.3", {"start": v(688.98, 712.72) * mm, "end": v(688.98, 404.88) * mm});
            skLineSegment(sketch, "E105.direction1", {"start": v(-352.43, 404.88) * mm, "end": v(384.18, 404.88) * mm, "construction": true});
            skSolve(sketch);
        }
        {
            var Q0;
            Q0 = qSketchRegion(id + "F19", true);
            extrude(context, id + "F20", {"entities" : qUnion([Q0]), "depth" : 19.05 * mm});
        }
        {
            var Q0;
            Q0=makeQuery(id+"F20.opExtrude","CAP_FACE",FACE,{"disambiguationData":[OSD([sQuery(id+"F19.wireOp",EDGE,"E104.bottom"),sQuery(id+"F19.wireOp",EDGE,"E104.top"),sQuery(id+"F19.wireOp",EDGE,"E104.left"),sQuery(id+"F19.wireOp",EDGE,"E104.right")])],"isStart":false});
            var sketch = newSketch(context, id + "F21", { "sketchPlane" : qUnion([Q0])});
            skLineSegment(sketch, "E106", {"start": v(-352.43, 712.72) * mm, "end": v(-47.62, 404.88) * mm, "construction": true});
            skLineSegment(sketch, "E107.bottom", {"start": v(-269.18, 628.65) * mm, "end": v(-130.87, 628.65) * mm, "construction": true});
            skLineSegment(sketch, "E107.top", {"start": v(-269.18, 488.95) * mm, "end": v(-130.87, 488.95) * mm, "construction": true});
            skLineSegment(sketch, "E107.left", {"start": v(-269.18, 628.65) * mm, "end": v(-269.18, 488.95) * mm, "construction": true});
            skLineSegment(sketch, "E107.right", {"start": v(-130.87, 628.65) * mm, "end": v(-130.87, 488.95) * mm, "construction": true});
            skPoint(sketch, "E107.middle", {"position": v(-200.02, 558.8) * mm});
            skPoint(sketch, "E108", {"position": v(-269.18, 628.65) * mm});
            skPoint(sketch, "E109", {"position": v(-130.87, 628.65) * mm});
            skPoint(sketch, "E110", {"position": v(-130.87, 488.95) * mm});
            skPoint(sketch, "E111", {"position": v(-269.18, 488.95) * mm});
            skLineSegment(sketch, "E112.1.0.0", {"start": v(467.42, 628.65) * mm, "end": v(605.73, 628.65) * mm, "construction": true});
            skLineSegment(sketch, "E112.1.0.1", {"start": v(605.73, 628.65) * mm, "end": v(605.73, 488.95) * mm, "construction": true});
            skLineSegment(sketch, "E112.1.0.2", {"start": v(467.42, 488.95) * mm, "end": v(605.73, 488.95) * mm, "construction": true});
            skPoint(sketch, "E112.1.0.3", {"position": v(467.42, 488.95) * mm});
            skPoint(sketch, "E112.1.0.4", {"position": v(467.42, 628.65) * mm});
            skPoint(sketch, "E112.1.0.5", {"position": v(605.73, 628.65) * mm});
            skPoint(sketch, "E112.1.0.6", {"position": v(605.73, 488.95) * mm});
            skPoint(sketch, "E112.1.0.7", {"position": v(536.57, 558.8) * mm});
            skLineSegment(sketch, "E112.1.0.8", {"start": v(467.42, 628.65) * mm, "end": v(467.42, 488.95) * mm, "construction": true});
            skLineSegment(sketch, "E112.direction1", {"start": v(-269.18, 488.95) * mm, "end": v(467.42, 488.95) * mm, "construction": true});
            skSolve(sketch);
        }
        {
            var Q0;
            Q0=sQuery(id+"F21.wireOp",VERTEX,"E108");
            var Q1;
            Q1=sQuery(id+"F21.wireOp",VERTEX,"E109");
            var Q2;
            Q2=sQuery(id+"F21.wireOp",VERTEX,"E111");
            var Q3;
            Q3=sQuery(id+"F21.wireOp",VERTEX,"E110");
            var Q4;
            Q4=sQuery(id+"F21.wireOp",VERTEX,"E112.1.0.4");
            var Q5;
            Q5=sQuery(id+"F21.wireOp",VERTEX,"E112.1.0.5");
            var Q6;
            Q6=sQuery(id+"F21.wireOp",VERTEX,"E112.1.0.6");
            var Q7;
            Q7=sQuery(id+"F21.wireOp",VERTEX,"E112.1.0.3");
            var Q8;
            Q8=makeQuery(id+"F20.opExtrude","SWEPT_BODY",BODY,{"disambiguationData":[OSD([sQuery(id+"F19.wireOp",EDGE,"E104.bottom"),sQuery(id+"F19.wireOp",EDGE,"E104.top"),sQuery(id+"F19.wireOp",EDGE,"E104.left"),sQuery(id+"F19.wireOp",EDGE,"E104.right")])]});
            var Q9;
            Q9=makeQuery(id+"F20.opExtrude","SWEPT_BODY",BODY,{"disambiguationData":[OSD([sQuery(id+"F19.wireOp",EDGE,"E105.1.0.0"),sQuery(id+"F19.wireOp",EDGE,"E105.1.0.1"),sQuery(id+"F19.wireOp",EDGE,"E105.1.0.2"),sQuery(id+"F19.wireOp",EDGE,"E105.1.0.3")])]});
            hole(context, id + "F22", {"style" : HoleStyle.SIMPLE, "endStyle" : HoleEndStyle.THROUGH, "holeDiameter" : 28.45 * mm, "locations" : qUnion([Q0, Q1, Q2, Q3, Q4, Q5, Q6, Q7]), "scope" : qUnion([Q8, Q9]), "isTappedThrough" : true});
        }
        {
            var Q0;
            Q0=makeQuery(id+"F1.opExtrude","SWEPT_BODY",BODY,{"disambiguationData":[OSD([sQuery(id+"F0.wireOp",EDGE,"E0.bottom"),sQuery(id+"F0.wireOp",EDGE,"E0.top"),sQuery(id+"F0.wireOp",EDGE,"E0.left"),sQuery(id+"F0.wireOp",EDGE,"E0.right"),sQuery(id+"F0.wireOp",EDGE,"E1.0"),sQuery(id+"F0.wireOp",EDGE,"E3.MirrorCS"),sQuery(id+"F0.wireOp",EDGE,"E5.0"),sQuery(id+"F0.wireOp",EDGE,"E6.MirrorCS"),sQuery(id+"F0.wireOp",EDGE,"E9.trimOffspring"),sQuery(id+"F0.wireOp",EDGE,"E11.trimOffspring"),sQuery(id+"F0.wireOp",EDGE,"E13.trimOffspring"),sQuery(id+"F0.wireOp",EDGE,"E14.trimOffspring"),sQuery(id+"F0.wireOp",EDGE,"E15.filletArc"),sQuery(id+"F0.wireOp",EDGE,"E16.filletArc"),sQuery(id+"F0.wireOp",EDGE,"E17.filletArc"),sQuery(id+"F0.wireOp",EDGE,"E18.filletArc")])]});
            var Q1;
            Q1=makeQuery(id+"F18.opExtrude","SWEPT_BODY",BODY,{"disambiguationData":[OSD([sQuery(id+"F17.wireOp",EDGE,"E89.bottom"),sQuery(id+"F17.wireOp",EDGE,"E89.top"),sQuery(id+"F17.wireOp",EDGE,"E89.left"),sQuery(id+"F17.wireOp",EDGE,"E89.right"),sQuery(id+"F17.wireOp",EDGE,"E90.0"),sQuery(id+"F17.wireOp",EDGE,"E91.0"),sQuery(id+"F17.wireOp",EDGE,"E92.0"),sQuery(id+"F17.wireOp",EDGE,"E94.MirrorCS"),sQuery(id+"F17.wireOp",EDGE,"E95.trimOffspring"),sQuery(id+"F17.wireOp",EDGE,"E96.trimOffspring"),sQuery(id+"F17.wireOp",EDGE,"E97.trimOffspring"),sQuery(id+"F17.wireOp",EDGE,"E98.trimOffspring"),sQuery(id+"F17.wireOp",EDGE,"E99.filletArc"),sQuery(id+"F17.wireOp",EDGE,"E100.filletArc"),sQuery(id+"F17.wireOp",EDGE,"E101.filletArc"),sQuery(id+"F17.wireOp",EDGE,"E102.filletArc")])]});
            var Q2;
            Q2=makeQuery(id+"F20.opExtrude","SWEPT_BODY",BODY,{"disambiguationData":[OSD([sQuery(id+"F19.wireOp",EDGE,"E104.bottom"),sQuery(id+"F19.wireOp",EDGE,"E104.top"),sQuery(id+"F19.wireOp",EDGE,"E104.left"),sQuery(id+"F19.wireOp",EDGE,"E104.right")])]});
            var Q3;
            Q3=makeQuery(id+"F18.opExtrude","SWEPT_BODY",BODY,{"disambiguationData":[OSD([sQuery(id+"F17.wireOp",EDGE,"E103.1.0.0"),sQuery(id+"F17.wireOp",EDGE,"E103.1.0.1"),sQuery(id+"F17.wireOp",EDGE,"E103.1.0.2"),sQuery(id+"F17.wireOp",EDGE,"E103.1.0.3"),sQuery(id+"F17.wireOp",EDGE,"E103.1.0.4"),sQuery(id+"F17.wireOp",EDGE,"E103.1.0.5"),sQuery(id+"F17.wireOp",EDGE,"E103.1.0.6"),sQuery(id+"F17.wireOp",EDGE,"E103.1.0.7"),sQuery(id+"F17.wireOp",EDGE,"E103.1.0.8"),sQuery(id+"F17.wireOp",EDGE,"E103.1.0.10"),sQuery(id+"F17.wireOp",EDGE,"E103.1.0.15"),sQuery(id+"F17.wireOp",EDGE,"E103.1.0.16"),sQuery(id+"F17.wireOp",EDGE,"E103.1.0.17"),sQuery(id+"F17.wireOp",EDGE,"E103.1.0.18"),sQuery(id+"F17.wireOp",EDGE,"E103.1.0.19"),sQuery(id+"F17.wireOp",EDGE,"E103.1.0.20")])]});
            var Q4;
            Q4=makeQuery(id+"F20.opExtrude","SWEPT_BODY",BODY,{"disambiguationData":[OSD([sQuery(id+"F19.wireOp",EDGE,"E105.1.0.0"),sQuery(id+"F19.wireOp",EDGE,"E105.1.0.1"),sQuery(id+"F19.wireOp",EDGE,"E105.1.0.2"),sQuery(id+"F19.wireOp",EDGE,"E105.1.0.3")])]});
            booleanBodies(context, id + "F23", {"operationType" : BooleanOperationType.UNION, "tools" : qUnion([Q0, Q1, Q2, Q3, Q4])});
        }
        {
            var Q0;
            {var subQ13=sQuery(id+"F0.wireOp",EDGE,"E13.trimOffspring");var subQ22=sQuery(id+"F0.wireOp",EDGE,"E0.top");Q0=makeQuery(id+"F23.opBoolean","SPLIT",FACE,{"disambiguationData":[TD([makeQuery(id+"F1.opExtrude","SWEPT_FACE",FACE,{"disambiguationData":[OSD([subQ13])]})])],"derivedFrom":makeQuery(id+"F8.opBoolean","MERGE",FACE,{"derivedFrom":[makeQuery(id+"F1.opExtrude","SWEPT_FACE",FACE,{"disambiguationData":[OSD([subQ22])]}),makeQuery(id+"F5.opExtrude","SWEPT_FACE",FACE,{"disambiguationData":[OSD([sQuery(id+"F4.wireOp",EDGE,"E39.top")])]}),makeQuery(id+"F5.opExtrude","SWEPT_FACE",FACE,{"disambiguationData":[OSD([sQuery(id+"F4.wireOp",EDGE,"E56.1.0.8")])]}),makeQuery(id+"F7.opExtrude","SWEPT_FACE",FACE,{"disambiguationData":[OSD([sQuery(id+"F6.wireOp",EDGE,"E57.top")])]}),makeQuery(id+"F7.opExtrude","SWEPT_FACE",FACE,{"disambiguationData":[OSD([sQuery(id+"F6.wireOp",EDGE,"E58.1.0.1")])]})]})});}
            var sketch = newSketch(context, id + "F24", { "sketchPlane" : qUnion([Q0])});
            skLineSegment(sketch, "E113.0", {"start": v(-352.43, 404.88) * mm, "end": v(-47.62, 404.88) * mm, "construction": true});
            skLineSegment(sketch, "E114", {"start": v(-200.02, 404.88) * mm, "end": v(-200.02, 233.55) * mm, "construction": true});
            skLineSegment(sketch, "E115.0", {"start": v(-209.68, 404.88) * mm, "end": v(-209.68, 233.55) * mm, "construction": true});
            skLineSegment(sketch, "E116.bottom", {"start": v(-209.68, 404.88) * mm, "end": v(-190.63, 404.88) * mm});
            skLineSegment(sketch, "E116.top", {"start": v(-209.68, -52.32) * mm, "end": v(-190.63, -52.32) * mm});
            skLineSegment(sketch, "E116.left", {"start": v(-209.68, 404.88) * mm, "end": v(-209.68, -52.32) * mm});
            skLineSegment(sketch, "E116.right", {"start": v(-190.63, 404.88) * mm, "end": v(-190.63, -52.32) * mm});
            skLineSegment(sketch, "E117.1.0.0", {"start": v(545.97, 404.88) * mm, "end": v(545.97, -52.32) * mm});
            skLineSegment(sketch, "E117.1.0.1", {"start": v(526.92, 404.88) * mm, "end": v(526.92, -52.32) * mm});
            skLineSegment(sketch, "E117.1.0.2", {"start": v(384.17, 404.88) * mm, "end": v(688.97, 404.88) * mm, "construction": true});
            skLineSegment(sketch, "E117.1.0.3", {"start": v(526.92, 404.88) * mm, "end": v(526.92, 233.55) * mm, "construction": true});
            skLineSegment(sketch, "E117.1.0.4", {"start": v(526.92, -52.32) * mm, "end": v(545.97, -52.32) * mm});
            skLineSegment(sketch, "E117.1.0.5", {"start": v(536.57, 404.88) * mm, "end": v(536.57, 233.55) * mm, "construction": true});
            skLineSegment(sketch, "E117.1.0.6", {"start": v(526.92, 404.88) * mm, "end": v(545.97, 404.88) * mm});
            skLineSegment(sketch, "E117.direction1", {"start": v(-209.68, -52.32) * mm, "end": v(526.92, -52.32) * mm, "construction": true});
            skSolve(sketch);
        }
        {
            var Q0;
            Q0 = qSketchRegion(id + "F24", true);
            extrude(context, id + "F25", {"entities" : qUnion([Q0]), "operationType" : NewBodyOperationType.ADD, "depth" : 168.4 * mm});
        }
        {
            var Q0;
            Q0=makeQuery(id+"F25.opExtrude","SWEPT_FACE",FACE,{"disambiguationData":[OSD([sQuery(id+"F24.wireOp",EDGE,"E117.1.0.0")])]});
            var sketch = newSketch(context, id + "F26", { "sketchPlane" : qUnion([Q0])});
            skLineSegment(sketch, "E118.0.0", {"start": v(52.32, -153.99) * mm, "end": v(-404.88, -153.99) * mm, "construction": true});
            skLineSegment(sketch, "E118.0.1", {"start": v(-404.88, -153.99) * mm, "end": v(-404.88, -322.39) * mm, "construction": true});
            skLineSegment(sketch, "E118.0.2", {"start": v(-404.88, -322.39) * mm, "end": v(52.32, -322.39) * mm, "construction": true});
            skLineSegment(sketch, "E118.0.3", {"start": v(52.32, -322.39) * mm, "end": v(52.32, -153.99) * mm, "construction": true});
            skLineSegment(sketch, "E119.0", {"start": v(52.32, -217.49) * mm, "end": v(-404.88, -217.49) * mm, "construction": true});
            skLineSegment(sketch, "E120", {"start": v(52.32, -217.49) * mm, "end": v(-404.88, -322.39) * mm});
            skLineSegment(sketch, "E121", {"start": v(52.32, -217.49) * mm, "end": v(52.32, -322.39) * mm});
            skLineSegment(sketch, "E122", {"start": v(52.32, -322.39) * mm, "end": v(-404.88, -322.39) * mm});
            skSolve(sketch);
        }
        {
            var Q0;
            Q0 = qSketchRegion(id + "F26", true);
            extrude(context, id + "F27", {"entities" : qUnion([Q0]), "operationType" : NewBodyOperationType.REMOVE, "endBound" : BoundingType.THROUGH_ALL, "oppositeDirection" : true, "depth" : 25.4 * mm});
        }
    });
